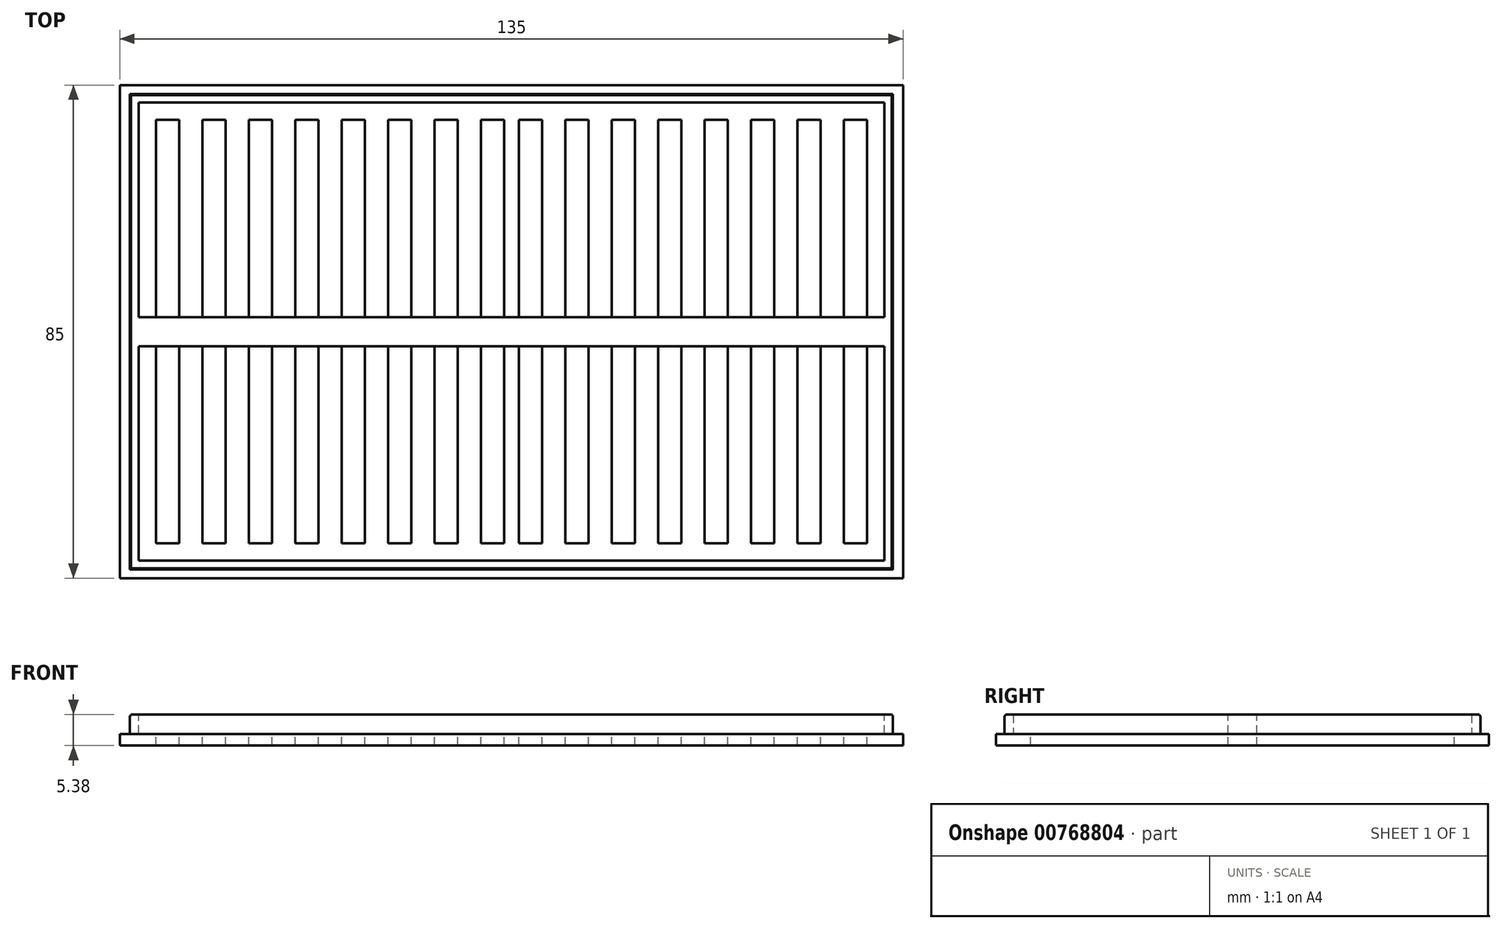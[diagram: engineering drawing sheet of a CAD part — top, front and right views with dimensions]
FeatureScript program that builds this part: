
annotation { "Feature Type Name" : "Feature", "Feature Type Description" : "" }
export const myFeature = defineFeature(function(context is Context, id is Id, definition is map)
    precondition{}
    {
        {
            var Q0;
            Q0=qCreatedBy(makeId("Top.planeOp"),FACE);
            var sketch = newSketch(context, id + "F0", { "sketchPlane" : qUnion([Q0])});
            skLineSegment(sketch, "E0.bottom", {"start": v(-67.5, 42.5) * mm, "end": v(67.5, 42.5) * mm});
            skLineSegment(sketch, "E0.top", {"start": v(-67.5, -42.5) * mm, "end": v(67.5, -42.5) * mm});
            skLineSegment(sketch, "E0.left", {"start": v(-67.5, 42.5) * mm, "end": v(-67.5, -42.5) * mm});
            skLineSegment(sketch, "E0.right", {"start": v(67.5, 42.5) * mm, "end": v(67.5, -42.5) * mm});
            skPoint(sketch, "E1", {"position": v(-67.5, 0) * mm});
            skPoint(sketch, "E2", {"position": v(0, 42.5) * mm});
            skSolve(sketch);
        }
        {
            var Q0;
            Q0 = qSketchRegion(id + "F0", true);
            extrude(context, id + "F1", {"entities" : qUnion([Q0]), "depth" : 2 * mm, "offsetDistance" : 25 * mm});
        }
        {
            var Q0;
            Q0=makeQuery(id+"F1.opExtrude","CAP_FACE",FACE,{"disambiguationData":[OSD([sQuery(id+"F0.wireOp",EDGE,"E0.bottom"),sQuery(id+"F0.wireOp",EDGE,"E0.top"),sQuery(id+"F0.wireOp",EDGE,"E0.left"),sQuery(id+"F0.wireOp",EDGE,"E0.right")])],"isStart":false});
            var sketch = newSketch(context, id + "F2", { "sketchPlane" : qUnion([Q0])});
            skLineSegment(sketch, "E3.bottom", {"start": v(-65.76, 41) * mm, "end": v(65.77, 41) * mm});
            skLineSegment(sketch, "E3.top", {"start": v(-65.77, -41) * mm, "end": v(65.77, -41) * mm});
            skLineSegment(sketch, "E3.left", {"start": v(-65.76, 41) * mm, "end": v(-65.77, -41) * mm});
            skLineSegment(sketch, "E3.right", {"start": v(65.77, 41) * mm, "end": v(65.77, -41) * mm});
            skLineSegment(sketch, "E4.bottom", {"start": v(-64.26, 39.5) * mm, "end": v(64.27, 39.5) * mm});
            skLineSegment(sketch, "E4.top", {"start": v(-64.27, -39.5) * mm, "end": v(64.27, -39.5) * mm});
            skLineSegment(sketch, "E4.left", {"start": v(-64.26, 39.5) * mm, "end": v(-64.27, -39.5) * mm});
            skLineSegment(sketch, "E4.right", {"start": v(64.27, 39.5) * mm, "end": v(64.27, -39.5) * mm});
            skSolve(sketch);
        }
        {
            var Q0;
            Q0 = qSketchRegion(id + "F2", true);
            extrude(context, id + "F3", {"entities" : qUnion([Q0]), "operationType" : NewBodyOperationType.ADD, "depth" : 3.38 * mm, "offsetDistance" : 25 * mm});
        }
        {
            var Q0;
            Q0=makeQuery(id+"F3.opExtrude","CAP_EDGE",EDGE,{"disambiguationData":[OSD([sQuery(id+"F2.wireOp",EDGE,"E3.left")])],"isStart":false});
            var Q1;
            Q1=makeQuery(id+"F3.opExtrude","CAP_EDGE",EDGE,{"disambiguationData":[OSD([sQuery(id+"F2.wireOp",EDGE,"E3.bottom")])],"isStart":false});
            var Q2;
            Q2=makeQuery(id+"F3.opExtrude","CAP_EDGE",EDGE,{"disambiguationData":[OSD([sQuery(id+"F2.wireOp",EDGE,"E3.top")])],"isStart":false});
            var Q3;
            Q3=makeQuery(id+"F3.opExtrude","CAP_EDGE",EDGE,{"disambiguationData":[OSD([sQuery(id+"F2.wireOp",EDGE,"E3.right")])],"isStart":false});
            chamfer(context, id + "F4", {"entities" : qUnion([Q0, Q1, Q2, Q3]), "chamferType" : ChamferType.OFFSET_ANGLE, "width" : 0.2 * mm, "oppositeDirection" : false, "angle" : 60 * degree, "tangentPropagation" : true});
        }
        {
            var Q0;
            {var subQ0=sQuery(id+"F2.wireOp",EDGE,"E3.right");Q0=makeQuery(id+"F4.opChamfer","BLEND_EDGE",EDGE,{"blendedFrom":[makeQuery(id+"F3.opExtrude","CAP_EDGE",EDGE,{"disambiguationData":[OSD([subQ0])],"isStart":false}),makeQuery(id+"F3.opExtrude","SWEPT_FACE",FACE,{"disambiguationData":[OSD([subQ0])]})],"blendedInto":[makeQuery(id+"F3.opExtrude","SWEPT_FACE",FACE,{"disambiguationData":[OSD([subQ0])]})]});}
            var Q1;
            {var subQ0=sQuery(id+"F2.wireOp",EDGE,"E3.bottom");Q1=makeQuery(id+"F4.opChamfer","BLEND_EDGE",EDGE,{"blendedFrom":[makeQuery(id+"F3.opExtrude","CAP_EDGE",EDGE,{"disambiguationData":[OSD([subQ0])],"isStart":false}),makeQuery(id+"F3.opExtrude","SWEPT_FACE",FACE,{"disambiguationData":[OSD([subQ0])]})],"blendedInto":[makeQuery(id+"F3.opExtrude","SWEPT_FACE",FACE,{"disambiguationData":[OSD([subQ0])]})]});}
            var Q2;
            {var subQ0=sQuery(id+"F2.wireOp",EDGE,"E3.top");Q2=makeQuery(id+"F4.opChamfer","BLEND_EDGE",EDGE,{"blendedFrom":[makeQuery(id+"F3.opExtrude","CAP_EDGE",EDGE,{"disambiguationData":[OSD([subQ0])],"isStart":false}),makeQuery(id+"F3.opExtrude","SWEPT_FACE",FACE,{"disambiguationData":[OSD([subQ0])]})],"blendedInto":[makeQuery(id+"F3.opExtrude","SWEPT_FACE",FACE,{"disambiguationData":[OSD([subQ0])]})]});}
            var Q3;
            {var subQ0=sQuery(id+"F2.wireOp",EDGE,"E3.left");Q3=makeQuery(id+"F4.opChamfer","BLEND_EDGE",EDGE,{"blendedFrom":[makeQuery(id+"F3.opExtrude","CAP_EDGE",EDGE,{"disambiguationData":[OSD([subQ0])],"isStart":false}),makeQuery(id+"F3.opExtrude","SWEPT_FACE",FACE,{"disambiguationData":[OSD([subQ0])]})],"blendedInto":[makeQuery(id+"F3.opExtrude","SWEPT_FACE",FACE,{"disambiguationData":[OSD([subQ0])]})]});}
            fillet(context, id + "F5", {"entities" : qUnion([Q0, Q1, Q2, Q3]), "radius" : 0.3 * mm, "tangentPropagation" : true, "allowEdgeOverflow" : false});
        }
        {
            var Q0;
            Q0=makeQuery(id+"F3.boolean.opBoolean","SPLIT",FACE,{"disambiguationData":[TD([makeQuery(id+"F3.opExtrude","SWEPT_FACE",FACE,{"disambiguationData":[OSD([sQuery(id+"F2.wireOp",EDGE,"E4.bottom")])]})])],"derivedFrom":makeQuery(id+"F1.opExtrude","CAP_FACE",FACE,{"disambiguationData":[OSD([sQuery(id+"F0.wireOp",EDGE,"E0.bottom"),sQuery(id+"F0.wireOp",EDGE,"E0.top"),sQuery(id+"F0.wireOp",EDGE,"E0.left"),sQuery(id+"F0.wireOp",EDGE,"E0.right")])],"isStart":false})});
            var sketch = newSketch(context, id + "F6", { "sketchPlane" : qUnion([Q0])});
            skLineSegment(sketch, "E5.bottom", {"start": v(-61.26, 36.5) * mm, "end": v(-57.26, 36.5) * mm});
            skLineSegment(sketch, "E5.top", {"start": v(-61.27, -36.5) * mm, "end": v(-57.27, -36.5) * mm});
            skLineSegment(sketch, "E5.left", {"start": v(-61.26, 36.5) * mm, "end": v(-61.27, -36.5) * mm});
            skLineSegment(sketch, "E5.right", {"start": v(-57.26, 36.5) * mm, "end": v(-57.27, -36.5) * mm});
            skLineSegment(sketch, "E6.1.0.0", {"start": v(-53.27, -36.5) * mm, "end": v(-49.27, -36.5) * mm});
            skLineSegment(sketch, "E6.1.0.1", {"start": v(-53.26, 36.5) * mm, "end": v(-53.27, -36.5) * mm});
            skLineSegment(sketch, "E6.1.0.2", {"start": v(-49.26, 36.5) * mm, "end": v(-49.27, -36.5) * mm});
            skLineSegment(sketch, "E6.1.0.3", {"start": v(-53.26, 36.5) * mm, "end": v(-49.26, 36.5) * mm});
            skLineSegment(sketch, "E6.2.0.0", {"start": v(-45.27, -36.5) * mm, "end": v(-41.27, -36.5) * mm});
            skLineSegment(sketch, "E6.2.0.1", {"start": v(-45.26, 36.5) * mm, "end": v(-45.27, -36.5) * mm});
            skLineSegment(sketch, "E6.2.0.2", {"start": v(-41.26, 36.5) * mm, "end": v(-41.27, -36.5) * mm});
            skLineSegment(sketch, "E6.2.0.3", {"start": v(-45.26, 36.5) * mm, "end": v(-41.26, 36.5) * mm});
            skLineSegment(sketch, "E6.3.0.0", {"start": v(-37.27, -36.5) * mm, "end": v(-33.27, -36.5) * mm});
            skLineSegment(sketch, "E6.3.0.1", {"start": v(-37.26, 36.5) * mm, "end": v(-37.27, -36.5) * mm});
            skLineSegment(sketch, "E6.3.0.2", {"start": v(-33.26, 36.5) * mm, "end": v(-33.27, -36.5) * mm});
            skLineSegment(sketch, "E6.3.0.3", {"start": v(-37.26, 36.5) * mm, "end": v(-33.26, 36.5) * mm});
            skLineSegment(sketch, "E6.4.0.0", {"start": v(-29.27, -36.5) * mm, "end": v(-25.27, -36.5) * mm});
            skLineSegment(sketch, "E6.4.0.1", {"start": v(-29.26, 36.5) * mm, "end": v(-29.27, -36.5) * mm});
            skLineSegment(sketch, "E6.4.0.2", {"start": v(-25.26, 36.5) * mm, "end": v(-25.27, -36.5) * mm});
            skLineSegment(sketch, "E6.4.0.3", {"start": v(-29.26, 36.5) * mm, "end": v(-25.26, 36.5) * mm});
            skLineSegment(sketch, "E6.5.0.0", {"start": v(-21.27, -36.5) * mm, "end": v(-17.27, -36.5) * mm});
            skLineSegment(sketch, "E6.5.0.1", {"start": v(-21.26, 36.5) * mm, "end": v(-21.27, -36.5) * mm});
            skLineSegment(sketch, "E6.5.0.2", {"start": v(-17.26, 36.5) * mm, "end": v(-17.27, -36.5) * mm});
            skLineSegment(sketch, "E6.5.0.3", {"start": v(-21.26, 36.5) * mm, "end": v(-17.26, 36.5) * mm});
            skLineSegment(sketch, "E6.6.0.0", {"start": v(-13.26, -36.5) * mm, "end": v(-9.27, -36.5) * mm});
            skLineSegment(sketch, "E6.6.0.1", {"start": v(-13.26, 36.5) * mm, "end": v(-13.27, -36.5) * mm});
            skLineSegment(sketch, "E6.6.0.2", {"start": v(-9.26, 36.5) * mm, "end": v(-9.27, -36.5) * mm});
            skLineSegment(sketch, "E6.6.0.3", {"start": v(-13.26, 36.5) * mm, "end": v(-9.26, 36.5) * mm});
            skLineSegment(sketch, "E6.7.0.0", {"start": v(-5.26, -36.5) * mm, "end": v(-1.27, -36.5) * mm});
            skLineSegment(sketch, "E6.7.0.1", {"start": v(-5.26, 36.5) * mm, "end": v(-5.27, -36.5) * mm});
            skLineSegment(sketch, "E6.7.0.2", {"start": v(-1.26, 36.5) * mm, "end": v(-1.26, -36.5) * mm});
            skLineSegment(sketch, "E6.7.0.3", {"start": v(-5.26, 36.5) * mm, "end": v(-1.26, 36.5) * mm});
            skLineSegment(sketch, "E6.direction1", {"start": v(-61.27, -36.5) * mm, "end": v(-53.27, -36.5) * mm, "construction": true});
            skLineSegment(sketch, "E7.MirrorCS", {"start": v(37.27, -36.5) * mm, "end": v(33.27, -36.5) * mm});
            skLineSegment(sketch, "E8.MirrorCS", {"start": v(45.26, 36.5) * mm, "end": v(41.26, 36.5) * mm});
            skLineSegment(sketch, "E9.MirrorCS", {"start": v(45.27, -36.5) * mm, "end": v(41.27, -36.5) * mm});
            skLineSegment(sketch, "E10.MirrorCS", {"start": v(53.26, 36.5) * mm, "end": v(49.26, 36.5) * mm});
            skLineSegment(sketch, "E11.MirrorCS", {"start": v(5.26, 36.5) * mm, "end": v(1.26, 36.5) * mm});
            skLineSegment(sketch, "E12.MirrorCS", {"start": v(53.27, -36.5) * mm, "end": v(49.27, -36.5) * mm});
            skLineSegment(sketch, "E13.MirrorCS", {"start": v(61.27, -36.5) * mm, "end": v(57.27, -36.5) * mm});
            skLineSegment(sketch, "E14.MirrorCS", {"start": v(61.26, 36.5) * mm, "end": v(57.26, 36.5) * mm});
            skLineSegment(sketch, "E15.MirrorCS", {"start": v(37.26, 36.5) * mm, "end": v(33.26, 36.5) * mm});
            skLineSegment(sketch, "E16.MirrorCS", {"start": v(13.26, -36.5) * mm, "end": v(9.27, -36.5) * mm});
            skLineSegment(sketch, "E17.MirrorCS", {"start": v(5.26, -36.5) * mm, "end": v(1.27, -36.5) * mm});
            skLineSegment(sketch, "E18.MirrorCS", {"start": v(21.26, 36.5) * mm, "end": v(17.26, 36.5) * mm});
            skLineSegment(sketch, "E19.MirrorCS", {"start": v(21.27, -36.5) * mm, "end": v(17.27, -36.5) * mm});
            skLineSegment(sketch, "E20.MirrorCS", {"start": v(13.26, 36.5) * mm, "end": v(9.26, 36.5) * mm});
            skLineSegment(sketch, "E21.MirrorCS", {"start": v(29.27, -36.5) * mm, "end": v(25.27, -36.5) * mm});
            skLineSegment(sketch, "E22.MirrorCS", {"start": v(29.26, 36.5) * mm, "end": v(25.26, 36.5) * mm});
            skLineSegment(sketch, "E23.MirrorCS", {"start": v(61.27, -36.5) * mm, "end": v(53.27, -36.5) * mm, "construction": true});
            skLineSegment(sketch, "E24.MirrorCS", {"start": v(41.26, 36.5) * mm, "end": v(41.27, -36.5) * mm});
            skLineSegment(sketch, "E25.MirrorCS", {"start": v(45.26, 36.5) * mm, "end": v(45.27, -36.5) * mm});
            skLineSegment(sketch, "E26.MirrorCS", {"start": v(25.26, 36.5) * mm, "end": v(25.27, -36.5) * mm});
            skLineSegment(sketch, "E27.MirrorCS", {"start": v(49.26, 36.5) * mm, "end": v(49.27, -36.5) * mm});
            skLineSegment(sketch, "E28.MirrorCS", {"start": v(53.26, 36.5) * mm, "end": v(53.27, -36.5) * mm});
            skLineSegment(sketch, "E29.MirrorCS", {"start": v(17.26, 36.5) * mm, "end": v(17.27, -36.5) * mm});
            skLineSegment(sketch, "E30.MirrorCS", {"start": v(57.26, 36.5) * mm, "end": v(57.27, -36.5) * mm});
            skLineSegment(sketch, "E31.MirrorCS", {"start": v(61.26, 36.5) * mm, "end": v(61.27, -36.5) * mm});
            skLineSegment(sketch, "E32.MirrorCS", {"start": v(13.26, 36.5) * mm, "end": v(13.27, -36.5) * mm});
            skLineSegment(sketch, "E33.MirrorCS", {"start": v(33.26, 36.5) * mm, "end": v(33.27, -36.5) * mm});
            skLineSegment(sketch, "E34.MirrorCS", {"start": v(37.26, 36.5) * mm, "end": v(37.27, -36.5) * mm});
            skLineSegment(sketch, "E35.MirrorCS", {"start": v(21.26, 36.5) * mm, "end": v(21.27, -36.5) * mm});
            skLineSegment(sketch, "E36.MirrorCS", {"start": v(1.26, 36.5) * mm, "end": v(1.26, -36.5) * mm});
            skLineSegment(sketch, "E37.MirrorCS", {"start": v(29.26, 36.5) * mm, "end": v(29.27, -36.5) * mm});
            skLineSegment(sketch, "E38.MirrorCS", {"start": v(5.26, 36.5) * mm, "end": v(5.27, -36.5) * mm});
            skLineSegment(sketch, "E39.MirrorCS", {"start": v(9.26, 36.5) * mm, "end": v(9.27, -36.5) * mm});
            skSolve(sketch);
        }
        {
            var Q0;
            Q0 = qSketchRegion(id + "F6", true);
            extrude(context, id + "F7", {"entities" : qUnion([Q0]), "operationType" : NewBodyOperationType.REMOVE, "oppositeDirection" : true, "depth" : 25 * mm, "offsetDistance" : 25 * mm});
        }
        {
            var Q0;
            Q0=makeQuery(id+"F1.opExtrude","CAP_FACE",FACE,{"disambiguationData":[OSD([sQuery(id+"F0.wireOp",EDGE,"E0.bottom"),sQuery(id+"F0.wireOp",EDGE,"E0.top"),sQuery(id+"F0.wireOp",EDGE,"E0.left"),sQuery(id+"F0.wireOp",EDGE,"E0.right")])],"isStart":true});
            extrude(context, id + "F8", {"entities" : qUnion([Q0]), "operationType" : NewBodyOperationType.REMOVE, "oppositeDirection" : true, "depth" : 1 * mm, "offsetDistance" : 25 * mm});
        }
        {
            var Q0;
            Q0=makeQuery(id+"F8.boolean.opBoolean","COPY",FACE,{"derivedFrom":makeQuery(id+"F8.opExtrude","CAP_FACE",FACE,{"disambiguationData":[OSD([sQuery(id+"F0.wireOp",EDGE,"E0.bottom"),sQuery(id+"F0.wireOp",EDGE,"E0.top"),sQuery(id+"F0.wireOp",EDGE,"E0.left"),sQuery(id+"F0.wireOp",EDGE,"E0.right")])],"isStart":false})});
            extrude(context, id + "F9", {"entities" : qUnion([Q0]), "operationType" : NewBodyOperationType.ADD, "depth" : 1 * mm, "offsetDistance" : 25 * mm});
        }
        {
            var Q0;
            Q0=makeQuery(id+"F3.opExtrude","CAP_FACE",FACE,{"disambiguationData":[OSD([sQuery(id+"F2.wireOp",EDGE,"E3.bottom"),sQuery(id+"F2.wireOp",EDGE,"E3.top"),sQuery(id+"F2.wireOp",EDGE,"E3.left"),sQuery(id+"F2.wireOp",EDGE,"E3.right"),sQuery(id+"F2.wireOp",EDGE,"E4.bottom"),sQuery(id+"F2.wireOp",EDGE,"E4.top"),sQuery(id+"F2.wireOp",EDGE,"E4.left"),sQuery(id+"F2.wireOp",EDGE,"E4.right")])],"isStart":false});
            var sketch = newSketch(context, id + "F10", { "sketchPlane" : qUnion([Q0])});
            skLineSegment(sketch, "E40.bottom", {"start": v(-64.27, 2.5) * mm, "end": v(64.27, 2.5) * mm});
            skLineSegment(sketch, "E40.top", {"start": v(-64.27, -2.5) * mm, "end": v(64.27, -2.5) * mm});
            skLineSegment(sketch, "E40.left", {"start": v(-64.27, 2.5) * mm, "end": v(-64.27, -2.5) * mm});
            skLineSegment(sketch, "E40.right", {"start": v(64.27, 2.5) * mm, "end": v(64.27, -2.5) * mm});
            skPoint(sketch, "E41", {"position": v(-64.27, 0) * mm});
            skSolve(sketch);
        }
        {
            var Q0;
            Q0 = qSketchRegion(id + "F10", true);
            var Q1;
            Q1=makeQuery(id+"F9.opExtrude","CAP_FACE",FACE,{"disambiguationData":[OSD([sQuery(id+"F0.wireOp",EDGE,"E0.bottom"),sQuery(id+"F0.wireOp",EDGE,"E0.top"),sQuery(id+"F0.wireOp",EDGE,"E0.left"),sQuery(id+"F0.wireOp",EDGE,"E0.right")])],"isStart":false});
            extrude(context, id + "F11", {"entities" : qUnion([Q0]), "operationType" : NewBodyOperationType.ADD, "endBound" : BoundingType.UP_TO_SURFACE, "oppositeDirection" : true, "depth" : 25 * mm, "endBoundEntityFace" : qUnion([Q1]), "offsetDistance" : 25 * mm});
        }
    });
